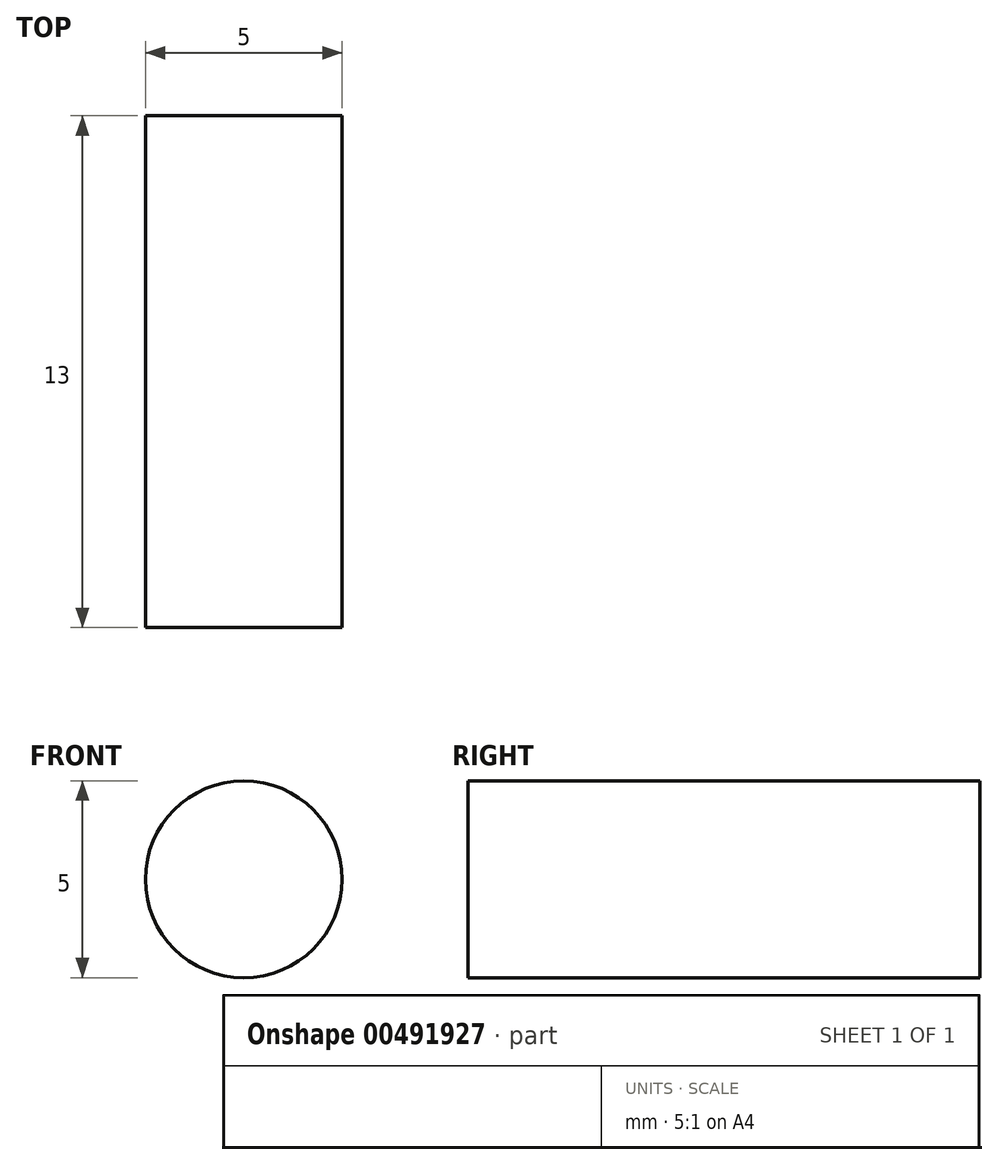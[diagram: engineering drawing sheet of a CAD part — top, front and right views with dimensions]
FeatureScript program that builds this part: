
annotation { "Feature Type Name" : "Feature", "Feature Type Description" : "" }
export const myFeature = defineFeature(function(context is Context, id is Id, definition is map)
    precondition{}
    {
        {
            assignVariable(context, id + "F0", {"name" : "depth", "anyValue" : 13});
        }
        {
            var Q0;
            Q0=qCreatedBy(makeId("Front.planeOp"),FACE);
            var sketch = newSketch(context, id + "F1", { "sketchPlane" : qUnion([Q0])});
            skCircle(sketch, "E0", {"center": v(0, 0) * mm, "radius": 2.5 * mm});
            skSolve(sketch);
        }
        {
            var Q0;
            Q0=makeQuery(id+"F1.imprint","IMPRINT",FACE,{"disambiguationData":[TD([[makeQuery(id+"F1.imprint","IMPRINT",EDGE,{"derivedFrom":sQuery(id+"F1.wireOp",EDGE,"E0")}),1.0]])]});
            extrude(context, id + "F2", {"entities" : qUnion([Q0]), "depth" : (getVariable(context, 'depth')) * mm});
        }
    });
